# Revit family: assa-abloy-sl500-ex-sw-r20
name_source: partatom
category: Doors
units: mm (PartAtom-declared; Revit-internal decimal feet)

## family parameters
Always vertical = Yes
Classification Number = 23.30.10.00
Cut with Voids When Loaded = No
Host = Wall
Room Calculation Point = No
Shared = No

## types (2) — shared parameters
Ctrl 2D Work Offset = 0"
Ctrl Pass Thru Work Offset = 1/2"
Ctrl Work Offset Main Door = 1 1/2"
Door Bottom Stile Height = 10"
Door Glazing Thickness = 3/4"
Door Mid Stile Height = 4"
Door Mid Stile Top = 38"
Door Thickness = 1 3/4"
Fire Rating = 0 Hour
Frame Depth = 4 1/2"
Frame Thickness = 1 3/4"
Function = Exterior
Height = 92"
Height R.O. = 1/2"
IFC Classification = Door
Manufacturer = ASSA ABLOY Entrance Systems
Masterformat 2014 Code = 08 42 29.23
Masterformat 2014 Description = Sliding Automatic Entrances
Maximium Opening = 30"
NBS Reference Code = 25-30-20-77
NBS Reference Description = Sliding Doorset Systems
OmniClass Code = 23-13 33 21 11 11
OmniClass Description = Automatic Aluminum-Framed Entrances
Automatic Aluminum-Framed Entrances
Automatic Aluminum-Framed Entrances
Operation = Exterior Entrance Door
Product Group = Overhead Concealed
Rough Height = 92 1/2"
Service Opening Height = 32 3/4"
Side Mullion Width = 2 5/8"
Thickness = 1 3/4"
URL = http://www.assaabloyentrance.com
Uniclass 1.4 Code = Sliding
Uniclass 1.4 Description = L4133
Uniclass 2.0 Code = Sliding Doorset Systems
Uniclass 2.0 Description = SS-25-30-20-77
Version = 1.0
Wall Closure = By host
Width R.O. = 1/2"

## per-type parameters (varying)
| type | Ctrl Door Max Size | Ctrl Door Min Size | Door Width | Door Width Between 84" to 96" | Model | Pass Through Door Width | Rough Width | Width |
| 7'-0" Width | 96" | 84" | 20 11/16" | 84" | SL500 EX-SW | 19 9/16" | 84 1/2" | 84" |
| 8'-0" Width | 0" | 0" | 23 11/16" | 96" | SL500 EX-SL | 22 9/16" | 96 1/2" | 96" |

## geometry (parser evidence)
native form markers: Sweep x4
no freeform markers — native parametric forms only
